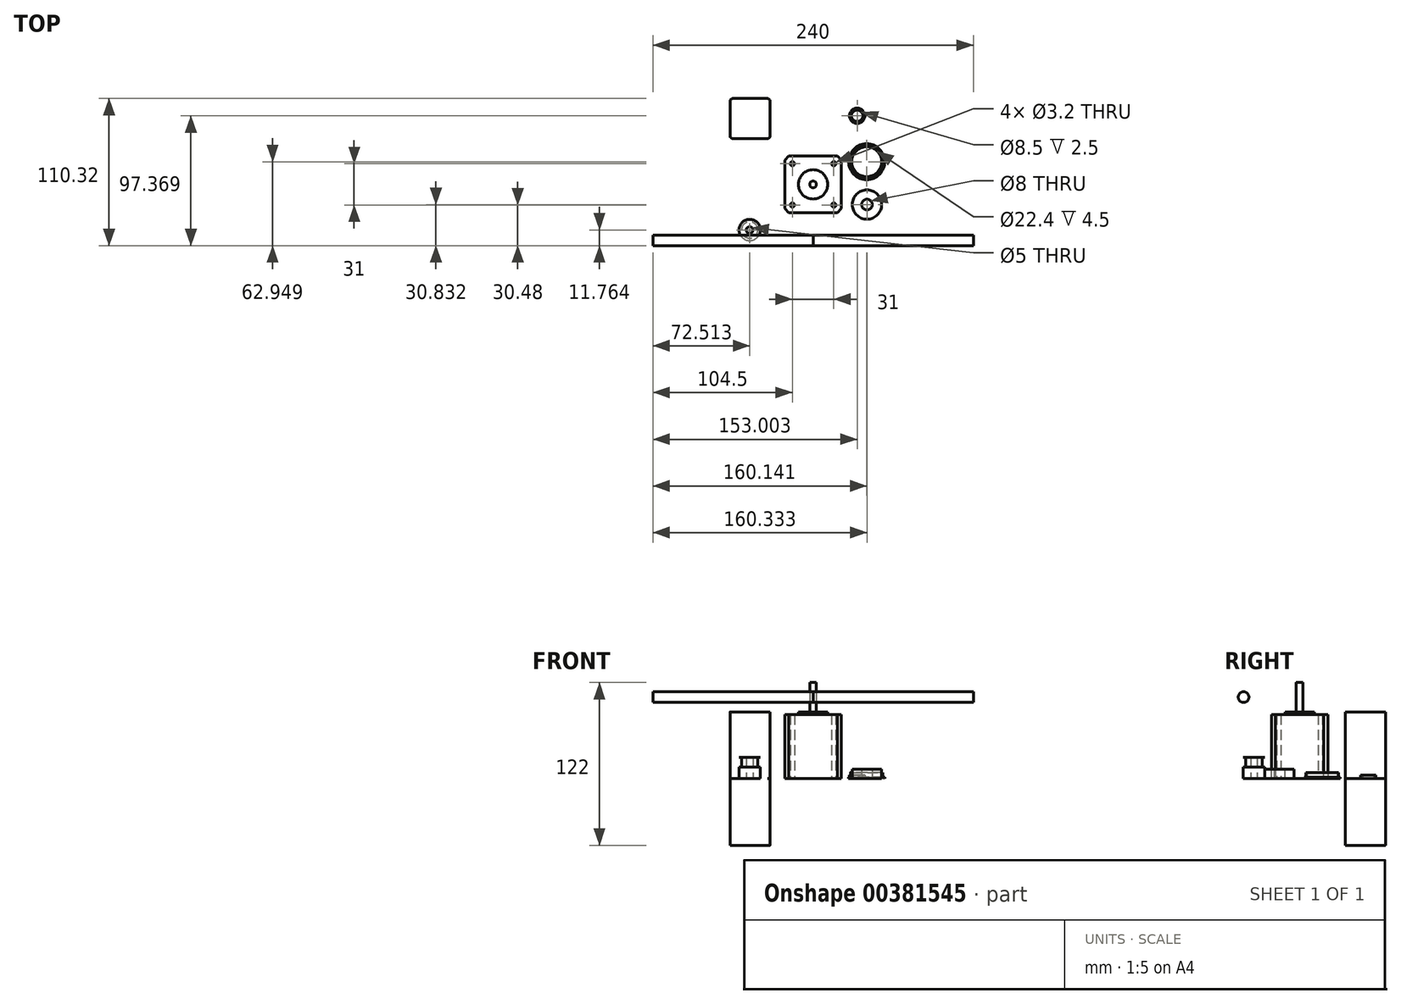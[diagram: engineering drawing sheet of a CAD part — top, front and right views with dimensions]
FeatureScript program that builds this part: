
annotation { "Feature Type Name" : "Feature", "Feature Type Description" : "" }
export const myFeature = defineFeature(function(context is Context, id is Id, definition is map)
    precondition{}
    {
        {
            var Q0;
            Q0=qCreatedBy(makeId("Top.planeOp"),FACE);
            var sketch = newSketch(context, id + "F0", { "sketchPlane" : qUnion([Q0])});
            skLineSegment(sketch, "E0.bottom", {"start": v(-21.15, 21.15) * mm, "end": v(21.15, 21.15) * mm});
            skLineSegment(sketch, "E0.top", {"start": v(-21.15, -21.15) * mm, "end": v(21.15, -21.15) * mm});
            skLineSegment(sketch, "E0.left", {"start": v(-21.15, 21.15) * mm, "end": v(-21.15, -21.15) * mm});
            skLineSegment(sketch, "E0.right", {"start": v(21.15, 21.15) * mm, "end": v(21.15, -21.15) * mm});
            skPoint(sketch, "E0.middle", {"position": v(0, 0) * mm});
            skLineSegment(sketch, "E1.bottom", {"start": v(-15.5, 15.5) * mm, "end": v(15.5, 15.5) * mm});
            skLineSegment(sketch, "E1.top", {"start": v(-15.5, -15.5) * mm, "end": v(15.5, -15.5) * mm});
            skLineSegment(sketch, "E1.left", {"start": v(-15.5, 15.5) * mm, "end": v(-15.5, -15.5) * mm});
            skLineSegment(sketch, "E1.right", {"start": v(15.5, 15.5) * mm, "end": v(15.5, -15.5) * mm});
            skCircle(sketch, "E2", {"center": v(-15.5, 15.5) * mm, "radius": 1.6 * mm});
            skCircle(sketch, "E3.1.0", {"center": v(-15.5, -15.5) * mm, "radius": 1.6 * mm});
            skCircle(sketch, "E3.2.0", {"center": v(15.5, -15.5) * mm, "radius": 1.6 * mm});
            skCircle(sketch, "E3.3.0", {"center": v(15.5, 15.5) * mm, "radius": 1.6 * mm});
            skSolve(sketch);
        }
        {
            var Q0;
            Q0=makeQuery(id+"F0.imprint","IMPRINT",FACE,{"disambiguationData":[TD([[makeQuery(id+"F0.imprint","IMPRINT",EDGE,{"derivedFrom":sQuery(id+"F0.wireOp",EDGE,"E0.bottom")}),-1.0]])]});
            var Q1;
            {var subQ5=sQuery(id+"F0.wireOp",EDGE,"E2");var subQ13=sQuery(id+"F0.wireOp",EDGE,"E1.bottom");var subQ14=makeQuery(id+"F0.imprint","INTERSECT",VERTEX,{"derivedFrom":[subQ13,subQ5]});Q1=makeQuery(id+"F0.imprint","IMPRINT",FACE,{"disambiguationData":[TD([[makeQuery(id+"F0.imprint","IMPRINT",EDGE,{"disambiguationData":[TD([[subQ14,-1.0]])],"derivedFrom":subQ13}),-1.0]])]});}
            extrude(context, id + "F1", {"entities" : qUnion([Q0, Q1]), "depth" : 48 * mm});
        }
        {
            var Q0;
            Q0=makeQuery(id+"F1.opExtrude","SWEPT_EDGE",EDGE,{"disambiguationData":[OSD([sQuery(id+"F0.wireOp",EDGE,"E0.bottom"),sQuery(id+"F0.wireOp",EDGE,"E0.left")])]});
            var Q1;
            Q1=makeQuery(id+"F1.opExtrude","SWEPT_EDGE",EDGE,{"disambiguationData":[OSD([sQuery(id+"F0.wireOp",EDGE,"E0.top"),sQuery(id+"F0.wireOp",EDGE,"E0.left")])]});
            var Q2;
            Q2=makeQuery(id+"F1.opExtrude","SWEPT_EDGE",EDGE,{"disambiguationData":[OSD([sQuery(id+"F0.wireOp",EDGE,"E0.bottom"),sQuery(id+"F0.wireOp",EDGE,"E0.right")])]});
            var Q3;
            Q3=makeQuery(id+"F1.opExtrude","SWEPT_EDGE",EDGE,{"disambiguationData":[OSD([sQuery(id+"F0.wireOp",EDGE,"E0.top"),sQuery(id+"F0.wireOp",EDGE,"E0.right")])]});
            chamfer(context, id + "F2", {"entities" : qUnion([Q0, Q1, Q2, Q3]), "width" : 3 * mm, "tangentPropagation" : true});
        }
        {
            var Q0;
            Q0=makeQuery(id+"F1.opExtrude","CAP_FACE",FACE,{"disambiguationData":[OSD([sQuery(id+"F0.wireOp",EDGE,"E0.bottom"),sQuery(id+"F0.wireOp",EDGE,"E0.top"),sQuery(id+"F0.wireOp",EDGE,"E0.left"),sQuery(id+"F0.wireOp",EDGE,"E0.right"),sQuery(id+"F0.wireOp",EDGE,"E2"),sQuery(id+"F0.wireOp",EDGE,"E3.1.0"),sQuery(id+"F0.wireOp",EDGE,"E3.2.0"),sQuery(id+"F0.wireOp",EDGE,"E3.3.0")])],"isStart":false});
            var sketch = newSketch(context, id + "F3", { "sketchPlane" : qUnion([Q0])});
            skCircle(sketch, "E4", {"center": v(0, 0) * mm, "radius": 2.5 * mm});
            skCircle(sketch, "E5", {"center": v(0, 0) * mm, "radius": 11 * mm});
            skSolve(sketch);
        }
        {
            var Q0;
            Q0=makeQuery(id+"F3.imprint","IMPRINT",FACE,{"disambiguationData":[TD([[makeQuery(id+"F3.imprint","IMPRINT",EDGE,{"derivedFrom":sQuery(id+"F3.wireOp",EDGE,"E4")}),-1.0]])]});
            extrude(context, id + "F4", {"entities" : qUnion([Q0]), "operationType" : NewBodyOperationType.ADD, "depth" : 2 * mm});
        }
        {
            var Q0;
            Q0=makeQuery(id+"F4.boolean.opBoolean","SPLIT",FACE,{"disambiguationData":[TD([makeQuery(id+"F4.opExtrude","SWEPT_FACE",FACE,{"disambiguationData":[OSD([sQuery(id+"F3.wireOp",EDGE,"E4")])]})])],"derivedFrom":makeQuery(id+"F1.opExtrude","CAP_FACE",FACE,{"disambiguationData":[OSD([sQuery(id+"F0.wireOp",EDGE,"E0.bottom"),sQuery(id+"F0.wireOp",EDGE,"E0.top"),sQuery(id+"F0.wireOp",EDGE,"E0.left"),sQuery(id+"F0.wireOp",EDGE,"E0.right"),sQuery(id+"F0.wireOp",EDGE,"E2"),sQuery(id+"F0.wireOp",EDGE,"E3.1.0"),sQuery(id+"F0.wireOp",EDGE,"E3.2.0"),sQuery(id+"F0.wireOp",EDGE,"E3.3.0")])],"isStart":false})});
            extrude(context, id + "F5", {"entities" : qUnion([Q0]), "operationType" : NewBodyOperationType.ADD, "depth" : 24 * mm});
        }
        {
            var Q0;
            Q0=qCreatedBy(makeId("Top.planeOp"),FACE);
            var sketch = newSketch(context, id + "F6", { "sketchPlane" : qUnion([Q0])});
            skCircle(sketch, "E6", {"center": v(-47.49, -34.22) * mm, "radius": 2.5 * mm});
            skCircle(sketch, "E7", {"center": v(-47.49, -34.22) * mm, "radius": 6.1 * mm});
            skCircle(sketch, "E8", {"center": v(-47.49, -34.22) * mm, "radius": 8 * mm});
            skSolve(sketch);
        }
        {
            var Q0;
            Q0=makeQuery(id+"F6.imprint","IMPRINT",FACE,{"disambiguationData":[TD([[makeQuery(id+"F6.imprint","IMPRINT",EDGE,{"derivedFrom":sQuery(id+"F6.wireOp",EDGE,"E6")}),-1.0]])]});
            extrude(context, id + "F7", {"entities" : qUnion([Q0]), "depth" : 16 * mm});
        }
        {
            var Q0;
            Q0=makeQuery(id+"F6.imprint","IMPRINT",FACE,{"disambiguationData":[TD([[makeQuery(id+"F6.imprint","IMPRINT",EDGE,{"derivedFrom":sQuery(id+"F6.wireOp",EDGE,"E7")}),-1.0]])]});
            extrude(context, id + "F8", {"entities" : qUnion([Q0]), "operationType" : NewBodyOperationType.ADD, "depth" : 8.5 * mm});
        }
        {
            var Q0;
            Q0=makeQuery(id+"F7.opExtrude","CAP_FACE",FACE,{"disambiguationData":[OSD([sQuery(id+"F6.wireOp",EDGE,"E6"),sQuery(id+"F6.wireOp",EDGE,"E7")])],"isStart":false});
            var sketch = newSketch(context, id + "F9", { "sketchPlane" : qUnion([Q0])});
            skCircle(sketch, "E9", {"center": v(-47.49, -34.22) * mm, "radius": 8 * mm});
            skSolve(sketch);
        }
        {
            var Q0;
            Q0=makeQuery(id+"F9.imprint","IMPRINT",FACE,{"disambiguationData":[TD([[makeQuery(id+"F9.imprint","IMPRINT",EDGE,{"derivedFrom":sQuery(id+"F9.wireOp",EDGE,"E9")}),1.0]])]});
            extrude(context, id + "F10", {"entities" : qUnion([Q0]), "operationType" : NewBodyOperationType.ADD, "oppositeDirection" : true, "depth" : .2 * mm});
        }
        {
            var Q0;
            Q0=qCreatedBy(makeId("Top.planeOp"),FACE);
            var sketch = newSketch(context, id + "F11", { "sketchPlane" : qUnion([Q0])});
            skCircle(sketch, "E10", {"center": v(40.14, 16.97) * mm, "radius": 11.2 * mm});
            skCircle(sketch, "E11", {"center": v(40.14, 16.97) * mm, "radius": 13.5 * mm});
            skCircle(sketch, "E12", {"center": v(40.14, 16.97) * mm, "radius": 12.2 * mm});
            skSolve(sketch);
        }
        {
            var Q0;
            Q0=makeQuery(id+"F11.imprint","IMPRINT",FACE,{"disambiguationData":[TD([[makeQuery(id+"F11.imprint","IMPRINT",EDGE,{"derivedFrom":sQuery(id+"F11.wireOp",EDGE,"E11")}),1.0]])]});
            extrude(context, id + "F12", {"entities" : qUnion([Q0]), "depth" : 1 * mm});
        }
        {
            var Q0;
            Q0=makeQuery(id+"F11.imprint","IMPRINT",FACE,{"disambiguationData":[TD([[makeQuery(id+"F11.imprint","IMPRINT",EDGE,{"derivedFrom":sQuery(id+"F11.wireOp",EDGE,"E10")}),-1.0]])]});
            extrude(context, id + "F13", {"entities" : qUnion([Q0]), "operationType" : NewBodyOperationType.ADD, "depth" : 4.5 * mm});
        }
        {
            var Q0;
            Q0=qCreatedBy(makeId("Top.planeOp"),FACE);
            var sketch = newSketch(context, id + "F14", { "sketchPlane" : qUnion([Q0])});
            skCircle(sketch, "E13", {"center": v(40.33, -15.15) * mm, "radius": 4 * mm});
            skCircle(sketch, "E14", {"center": v(40.33, -15.15) * mm, "radius": 11 * mm});
            skSolve(sketch);
        }
        {
            var Q0;
            Q0=makeQuery(id+"F14.imprint","IMPRINT",FACE,{"disambiguationData":[TD([[makeQuery(id+"F14.imprint","IMPRINT",EDGE,{"derivedFrom":sQuery(id+"F14.wireOp",EDGE,"E13")}),-1.0]])]});
            extrude(context, id + "F15", {"entities" : qUnion([Q0]), "depth" : 7 * mm});
        }
        {
            var Q0;
            Q0=qCreatedBy(makeId("Top.planeOp"),FACE);
            var sketch = newSketch(context, id + "F16", { "sketchPlane" : qUnion([Q0])});
            skCircle(sketch, "E15", {"center": v(33, 51.39) * mm, "radius": 4.25 * mm});
            skCircle(sketch, "E16", {"center": v(33, 51.39) * mm, "radius": 5.75 * mm});
            skSolve(sketch);
        }
        {
            var Q0;
            Q0=makeQuery(id+"F16.imprint","IMPRINT",FACE,{"disambiguationData":[TD([[makeQuery(id+"F16.imprint","IMPRINT",EDGE,{"derivedFrom":sQuery(id+"F16.wireOp",EDGE,"E15")}),-1.0]])]});
            extrude(context, id + "F17", {"entities" : qUnion([Q0]), "depth" : 2.5 * mm});
        }
        {
            var Q0;
            Q0=qCreatedBy(makeId("Right.planeOp"),FACE);
            var sketch = newSketch(context, id + "F18", { "sketchPlane" : qUnion([Q0])});
            skCircle(sketch, "E17", {"center": v(-41.98, 61.05) * mm, "radius": 4 * mm});
            skSolve(sketch);
        }
        {
            var Q0;
            Q0=makeQuery(id+"F18.imprint","IMPRINT",FACE,{"disambiguationData":[TD([[makeQuery(id+"F18.imprint","IMPRINT",EDGE,{"derivedFrom":sQuery(id+"F18.wireOp",EDGE,"E17")}),1.0]])]});
            extrude(context, id + "F19", {"entities" : qUnion([Q0]), "depth" : 120 * mm});
        }
        {
            var Q0;
            Q0=makeQuery(id+"F19.opExtrude","SWEPT_BODY",BODY,{"disambiguationData":[OSD([sQuery(id+"F18.wireOp",EDGE,"E17")])]});
            var Q1;
            Q1=qCreatedBy(makeId("Right.planeOp"),FACE);
            mirror(context, id + "F20", {"operationType" : NewBodyOperationType.ADD, "entities" : qUnion([Q0]), "mirrorPlane" : qUnion([Q1])});
        }
        {
            var Q0;
            Q0=qCreatedBy(makeId("Top.planeOp"),FACE);
            var sketch = newSketch(context, id + "F21", { "sketchPlane" : qUnion([Q0])});
            skLineSegment(sketch, "E18.bottom", {"start": v(-32.17, 64.34) * mm, "end": v(-62.17, 64.34) * mm});
            skLineSegment(sketch, "E18.top", {"start": v(-32.17, 34.34) * mm, "end": v(-62.17, 34.34) * mm});
            skLineSegment(sketch, "E18.left", {"start": v(-32.17, 64.34) * mm, "end": v(-32.17, 34.34) * mm});
            skLineSegment(sketch, "E18.right", {"start": v(-62.17, 64.34) * mm, "end": v(-62.17, 34.34) * mm});
            skPoint(sketch, "E18.middle", {"position": v(-47.17, 49.34) * mm});
            skSolve(sketch);
        }
        {
            var Q0;
            Q0=makeQuery(id+"F21.imprint","IMPRINT",FACE,{"disambiguationData":[TD([[makeQuery(id+"F21.imprint","IMPRINT",EDGE,{"derivedFrom":sQuery(id+"F21.wireOp",EDGE,"E18.bottom")}),1.0]])]});
            extrude(context, id + "F22", {"entities" : qUnion([Q0]), "depth" : 50 * mm});
        }
        {
            var Q0;
            Q0=makeQuery(id+"F22.opExtrude","SWEPT_EDGE",EDGE,{"disambiguationData":[OSD([sQuery(id+"F21.wireOp",EDGE,"E18.bottom"),sQuery(id+"F21.wireOp",EDGE,"E18.right")])]});
            var Q1;
            Q1=makeQuery(id+"F22.opExtrude","SWEPT_EDGE",EDGE,{"disambiguationData":[OSD([sQuery(id+"F21.wireOp",EDGE,"E18.top"),sQuery(id+"F21.wireOp",EDGE,"E18.right")])]});
            var Q2;
            Q2=makeQuery(id+"F22.opExtrude","SWEPT_EDGE",EDGE,{"disambiguationData":[OSD([sQuery(id+"F21.wireOp",EDGE,"E18.bottom"),sQuery(id+"F21.wireOp",EDGE,"E18.left")])]});
            var Q3;
            Q3=makeQuery(id+"F22.opExtrude","SWEPT_EDGE",EDGE,{"disambiguationData":[OSD([sQuery(id+"F21.wireOp",EDGE,"E18.top"),sQuery(id+"F21.wireOp",EDGE,"E18.left")])]});
            fillet(context, id + "F23", {"entities" : qUnion([Q0, Q1, Q2, Q3]), "radius" : 2 * mm, "tangentPropagation" : true, "allowEdgeOverflow" : false});
        }
        {
            var Q0;
            Q0=makeQuery(id+"F22.opExtrude","SWEPT_BODY",BODY,{"disambiguationData":[OSD([sQuery(id+"F21.wireOp",EDGE,"E18.bottom"),sQuery(id+"F21.wireOp",EDGE,"E18.top"),sQuery(id+"F21.wireOp",EDGE,"E18.left"),sQuery(id+"F21.wireOp",EDGE,"E18.right")])]});
            var Q1;
            Q1=qCreatedBy(makeId("Top.planeOp"),FACE);
            mirror(context, id + "F24", {"operationType" : NewBodyOperationType.ADD, "entities" : qUnion([Q0]), "mirrorPlane" : qUnion([Q1])});
        }
    });
